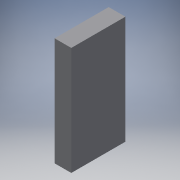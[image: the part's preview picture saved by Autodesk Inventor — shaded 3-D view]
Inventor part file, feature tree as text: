
AUTODESK INVENTOR PART (.ipt)
format: ipt  version: 2016 (Build 200138000, 138)  size: 84,992 bytes
history: native  units: in
note: dims shown in document units (in); Inventor stores cm internally (conversion verified against a paired STEP export)
features: extrude x1, sketch x1
ambient origin geometry x8: Origin, YZ Plane, XZ Plane, XY Plane, X Axis, Y Axis, Z Axis, Center Point
bodies: Solid1 (feature_tree)
feature tree (2):
  extrude  "Extrusion1"  Depth=0.4625in TaperAngle=0.0deg
  sketch  "Sketch1"  dims[d0=3.0in d1=0.4625in d2=0.0in]
